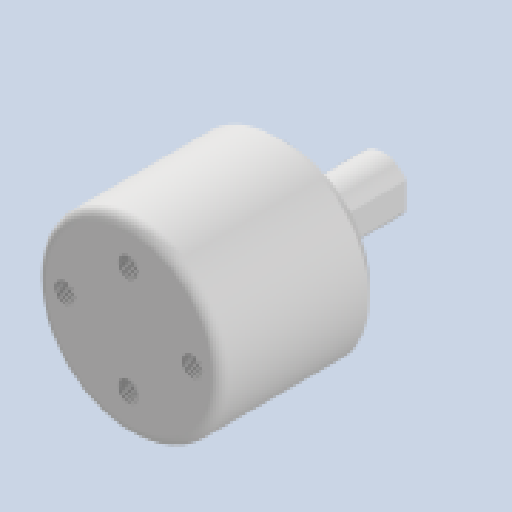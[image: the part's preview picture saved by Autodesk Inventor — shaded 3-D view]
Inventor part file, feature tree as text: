
AUTODESK INVENTOR PART (.ipt)
format: ipt  version: 2024 (Build 280153000, 153)  size: 164,864 bytes
history: native  units: mm
features: thread x4, extrude x3, sketch x3, fillet x1, chamfer x1
ambient origin geometry x8: Origin, YZ Plane, XZ Plane, XY Plane, X Axis, Y Axis, Z Axis, Center Point
bodies: Solid1 (feature_tree)
feature tree (12):
  extrude  "Extrusion1"  Depth=24.0mm TaperAngle=0.0deg
  fillet  "Fillet1"  Radius=1.5mm
  chamfer  "Chamfer1"  Distance=2.0mm Angle=45.0deg
  extrude  "Extrusion2"  Depth=6.8mm
  extrude  "Extrusion3"  Depth=4.0mm
  thread  "Thread1"  [1 undecoded]
  thread  "Thread2"  [1 undecoded]
  thread  "Thread3"  [1 undecoded]
  thread  "Thread4"  [1 undecoded]
  sketch  "Sketch1"  dims[d0=27.8mm d1=24.0mm d2=0.0mm d3=1.5mm d4=2.0mm d5=2.0mm d6=45.0deg]
  sketch  "Sketch2"  dims[d7=7.88mm d8=6.8mm]
  sketch  "Sketch3"  dims[d9=14.0mm d10=0.0mm d11=8.0mm d12=9.5mm d13=3.0mm d14=3.0mm d15=4.0mm d16=0.0mm d17=30.0mm d18=0.0mm d19=30.0mm d20=0.0mm d21=30.0mm d22=0.0mm d23=30.0mm d24=0.0mm]
note: 4 required parameter values undecoded (feature->parameter linkage not recoverable at this tier; creation-order binding heuristic only, values carry confidence <= 0.55)
